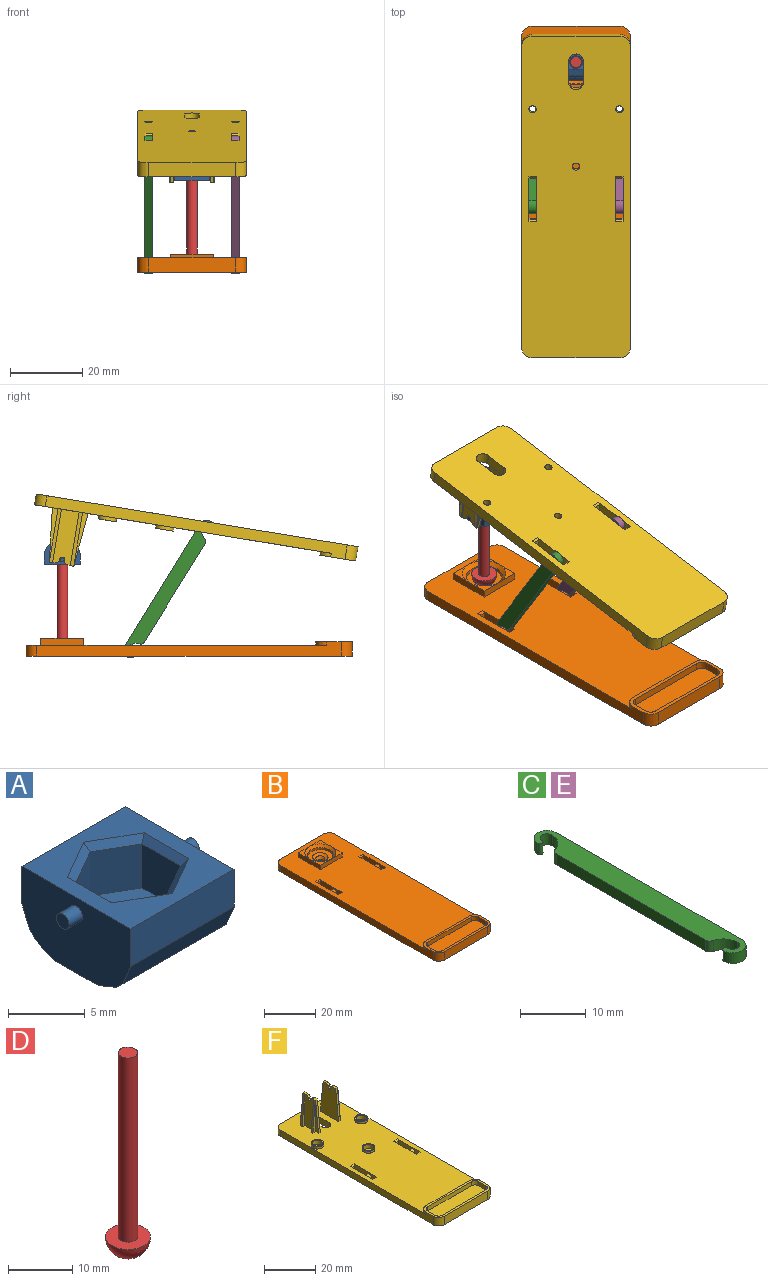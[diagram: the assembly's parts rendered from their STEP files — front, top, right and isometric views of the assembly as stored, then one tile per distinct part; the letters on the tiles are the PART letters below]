
ASSEMBLY  parts=6 mates=8
PART A: 30 faces, bbox 12x10x6 mm
  f0: plane 10x9.5mm, normal (0,0,1), area 51.6mm2, adj f3,f4,f5,f6,f24,f25,f26,f27
  f1: plane 1.15x1.15mm, normal (-1,0,0), area 1mm2, adj f2
  f2: cylinder r=0.57mm len=1.25mm, axis (1,0,0), area 4.5mm2, adj f1,f3
  f3: plane 10x6mm, normal (-1,0,0), area 53.5mm2, adj f0,f2,f4,f6,f7,f10,f11,f19
  f4: plane 9.5x3mm, normal (0,-1,0), area 28.5mm2, adj f0,f3,f5,f22
  f5: plane 10x6mm, normal (1,0,0), area 53.5mm2, adj f0,f4,f6,f7,f9,f10,f11,f19
  f6: plane 9.5x3mm, normal (0,1,0), area 28.5mm2, adj f0,f3,f5,f19
  f7: plane 9.5x4mm, normal (0,0,-1), area 28.4mm2, adj f3,f5,f20,f21,f23
  f8: plane 1.15x1.15mm, normal (1,0,0), area 1mm2, adj f9
  f9: cylinder r=0.57mm len=1.25mm, axis (1,0,0), area 4.5mm2, adj f5,f8
  f10: plane 9.5x0.59mm, normal (0,0.71,-0.71), area 7.9mm2, adj f3,f5,f19,f20
  f11: plane 9.5x0.59mm, normal (0,-0.71,-0.71), area 7.9mm2, adj f3,f5,f21,f22
  f12: plane 3.5x3.04mm, normal (-0.5,-0.87,0), area 12.3mm2, adj f13,f17,f18,f26
  f13: plane 3.5x3.04mm, normal (0.5,-0.87,0), area 12.3mm2, adj f12,f14,f18,f28
  f14: plane 3.51x3.5mm, normal (1,0,0), area 12.3mm2, adj f13,f15,f18,f29
  f15: plane 3.5x3.04mm, normal (0.5,0.87,0), area 12.3mm2, adj f14,f16,f18,f27
  f16: plane 3.5x3.04mm, normal (-0.5,0.87,0), area 12.3mm2, adj f15,f17,f18,f25
  f17: plane 3.51x3.5mm, normal (-1,0,0), area 12.3mm2, adj f12,f16,f18,f24
  f18: plane 7.02x6.08mm, normal (0,0,1), area 22.4mm2, adj f12,f13,f14,f15,f16,f17,f23
  f19: plane 9.5x1.71mm, normal (0,0.92,-0.38), area 17.6mm2, adj f3,f5,f6,f10
  f20: plane 9.5x1.71mm, normal (0,0.38,-0.92), area 17.6mm2, adj f3,f5,f7,f10
  f21: plane 9.5x1.71mm, normal (0,-0.38,-0.92), area 17.6mm2, adj f3,f5,f7,f11
  f22: plane 9.5x1.71mm, normal (0,-0.92,-0.38), area 17.6mm2, adj f3,f4,f5,f11
  f23: cylinder r=1.75mm len=3.5mm, axis (0,0,1), area 22mm2, adj f7,f18
  f24: plane 4.09x0.5mm, normal (-0.71,0,0.71), area 2.7mm2, adj f0,f17,f25,f26
  f25: plane 3.54x2.33mm, normal (-0.35,0.61,0.71), area 2.7mm2, adj f0,f16,f24,f27
  f26: plane 3.54x2.33mm, normal (-0.35,-0.61,0.71), area 2.7mm2, adj f0,f12,f24,f28
  f27: plane 3.54x2.33mm, normal (0.35,0.61,0.71), area 2.7mm2, adj f0,f15,f25,f29
  f28: plane 3.54x2.33mm, normal (0.35,-0.61,0.71), area 2.7mm2, adj f0,f13,f26,f29
  f29: plane 4.09x0.5mm, normal (0.71,0,0.71), area 2.7mm2, adj f0,f14,f27,f28
PART B: 56 faces, bbox 30x90x5 mm
  f0: plane 83x30mm, normal (0,0,1), area 2202.2mm2, adj f6,f8,f9,f12,f13,f14,f15,f16
  f1: plane 90x30mm, normal (0,0,-1), area 2631.5mm2, adj f6,f7,f8,f9,f10,f11,f12,f13
  f2: sphere r=5mm, area 21mm2, adj f32,f36
  f3: plane 6x6mm, normal (0,0,1), area 7.7mm2, adj f29,f30,f34
  f4: plane 6x6mm, normal (0,0,1), area 7.7mm2, adj f28,f29,f34
  f5: plane 6x6mm, normal (0,0,1), area 7.7mm2, adj f27,f28,f34
  f6: plane 84x4mm, normal (-1,0,0), area 256mm2, adj f0,f1,f10,f13,f16,f25
  f7: plane 24x4mm, normal (0,-1,0), area 96mm2, adj f1,f10,f11,f25
  f8: plane 84x4mm, normal (1,0,0), area 256mm2, adj f0,f1,f11,f12,f14,f25
  f9: plane 24x3mm, normal (0,1,0), area 72mm2, adj f0,f1,f12,f13
  f10: cylinder r=3mm len=4mm, axis (0,0,-1), area 18.8mm2, adj f1,f6,f7,f25
  f11: cylinder r=3mm len=4mm, axis (0,0,1), area 18.8mm2, adj f1,f7,f8,f25
  f12: cylinder r=3mm len=3mm, axis (0,0,-1), area 14.1mm2, adj f0,f1,f8,f9
  f13: cylinder r=3mm len=3mm, axis (0,0,1), area 14.1mm2, adj f0,f1,f6,f9
  f14: cylinder r=3mm len=3mm, axis (0,0,-1), area 4.7mm2, adj f0,f8,f15,f25
  f15: plane 24x1mm, normal (0,1,0), area 24mm2, adj f0,f14,f16,f25
  f16: cylinder r=3mm len=3mm, axis (0,0,-1), area 4.7mm2, adj f0,f6,f15,f25
  f17: plane 4x2mm, normal (-1,0,0), area 8mm2, adj f18,f24,f25,f26
  f18: cylinder r=2mm len=2mm, axis (0,0,-1), area 6.3mm2, adj f17,f19,f25,f26
  f19: plane 24x2mm, normal (0,1,0), area 48mm2, adj f18,f20,f25,f26
  f20: cylinder r=2mm len=2mm, axis (0,0,-1), area 6.3mm2, adj f19,f21,f25,f26
  f21: plane 4x2mm, normal (1,0,0), area 8mm2, adj f20,f22,f25,f26
  f22: cylinder r=2mm len=2mm, axis (0,0,-1), area 6.3mm2, adj f21,f23,f25,f26
  f23: plane 24x2mm, normal (0,-1,0), area 48mm2, adj f22,f24,f25,f26
  f24: cylinder r=2mm len=2mm, axis (0,0,-1), area 6.3mm2, adj f17,f23,f25,f26
  f25: plane 30x10mm, normal (0,0,1), area 71.7mm2, adj f6,f7,f8,f10,f11,f14,f15,f16
  f26: plane 28x8mm, normal (0,0,1), area 220.6mm2, adj f17,f18,f19,f20,f21,f22,f23,f24
  f27: plane 12x2mm, normal (0,1,0), area 24mm2, adj f0,f5,f28,f30,f31
  f28: plane 12x2mm, normal (-1,0,0), area 24mm2, adj f0,f4,f5,f27,f29
  f29: plane 12x2mm, normal (0,-1,0), area 24mm2, adj f0,f3,f4,f28,f30
  f30: plane 12x2mm, normal (1,0,0), area 24mm2, adj f0,f3,f27,f29,f31
  f31: plane 6x6mm, normal (0,0,1), area 7.7mm2, adj f27,f30,f34
  f32: plane 10x10mm, normal (0,0,1), area 50.3mm2, adj f2,f33
  f33: cylinder r=5mm len=10mm, axis (0,0,-1), area 31.4mm2, adj f32,f34
  f34: cone r=6mm half-angle=45deg, axis (0,0,1), area 48.9mm2, adj f3,f4,f5,f31,f33
  f35: cylinder r=1mm len=2mm, axis (0,0,1), area 4.3mm2, adj f36,f37
  f36: cone r=1.79mm half-angle=34.5deg, axis (0,0,1), area 12.2mm2, adj f2,f35
  f37: cone r=1mm half-angle=45deg, axis (0,0,-1), area 5.6mm2, adj f1,f35
  f38: plane 2.15x2mm, normal (0,-1,0), area 4.3mm2, adj f39,f40,f52,f53
  f39: plane 12.5x3mm, normal (-1,0,0), area 31.9mm2, adj f0,f1,f38,f41,f47,f52,f53,f54
  f40: plane 12.5x3mm, normal (1,0,0), area 31.9mm2, adj f0,f1,f38,f41,f47,f52,f53,f54
  f41: plane 2.15x2mm, normal (0,1,0), area 4.3mm2, adj f39,f40,f54,f55
  f42: plane 2.15x2mm, normal (0,1,0), area 4.3mm2, adj f43,f45,f49,f50
  f43: plane 12.5x3mm, normal (-1,0,0), area 31.9mm2, adj f0,f1,f42,f44,f46,f48,f49,f50
  f44: plane 2.15x2mm, normal (0,-1,0), area 4.3mm2, adj f43,f45,f48,f51
  f45: plane 12.5x3mm, normal (1,0,0), area 31.9mm2, adj f0,f1,f42,f44,f46,f48,f49,f50
  f46: cylinder r=1mm len=2.15mm, axis (-1,0,0), area 13.5mm2, adj f43,f45
  f47: cylinder r=1mm len=2.15mm, axis (-1,0,0), area 13.5mm2, adj f39,f40
  f48: plane 2.15x0.5mm, normal (0,-0.71,0.71), area 1.5mm2, adj f0,f43,f44,f45
  f49: plane 2.15x0.5mm, normal (0,0.71,0.71), area 1.5mm2, adj f0,f42,f43,f45
  f50: plane 2.15x0.5mm, normal (0,0.71,-0.71), area 1.5mm2, adj f1,f42,f43,f45
  f51: plane 2.15x0.5mm, normal (0,-0.71,-0.71), area 1.5mm2, adj f1,f43,f44,f45
  f52: plane 2.15x0.5mm, normal (0,-0.71,-0.71), area 1.5mm2, adj f1,f38,f39,f40
  f53: plane 2.15x0.5mm, normal (0,-0.71,0.71), area 1.5mm2, adj f0,f38,f39,f40
  f54: plane 2.15x0.5mm, normal (0,0.71,-0.71), area 1.5mm2, adj f1,f39,f40,f41
  f55: plane 2.15x0.5mm, normal (0,0.71,0.71), area 1.5mm2, adj f0,f39,f40,f41
PART C: 14 faces, bbox 4x44x2 mm
  f0: cylinder r=1.07mm len=2.15mm, axis (0,0,-1), area 6.8mm2, adj f1,f9,f10,f11
  f1: cylinder r=3.08mm len=2.98mm, axis (0,0,-1), area 8.1mm2, adj f0,f10,f11,f12
  f2: plane 32.1x2mm, normal (-1,0,0), area 64.2mm2, adj f10,f11,f12,f13
  f3: cylinder r=3.08mm len=2.98mm, axis (0,0,-1), area 8.1mm2, adj f4,f10,f11,f13
  f4: cylinder r=1.07mm len=2.15mm, axis (0,0,-1), area 6.8mm2, adj f3,f5,f10,f11
  f5: cylinder r=0.46mm len=2mm, axis (0,0,-1), area 2.9mm2, adj f4,f6,f10,f11
  f6: cylinder r=2mm len=4mm, axis (0,0,-1), area 12.6mm2, adj f5,f7,f10,f11
  f7: plane 40x2mm, normal (1,0,0), area 80mm2, adj f6,f8,f10,f11
  f8: cylinder r=2mm len=4mm, axis (0,0,-1), area 12.6mm2, adj f7,f9,f10,f11
  f9: cylinder r=0.46mm len=2mm, axis (0,0,-1), area 2.9mm2, adj f0,f8,f10,f11
  f10: plane 44x4mm, normal (0,0,1), area 154.5mm2, adj f0,f1,f2,f3,f4,f5,f6,f7
  f11: plane 44x4mm, normal (0,0,-1), area 154.5mm2, adj f0,f1,f2,f3,f4,f5,f6,f7
  f12: cylinder r=1mm len=2mm, axis (0,0,-1), area 2.6mm2, adj f1,f2,f10,f11
  f13: cylinder r=1mm len=2mm, axis (0,0,-1), area 2.6mm2, adj f2,f3,f10,f11
PART D: 4 faces, bbox 7x7x38.5 mm
  f0: cylinder r=1.5mm len=35mm, axis (0,0,-1), area 329.9mm2, adj f1,f3
  f1: plane 3x3mm, normal (0,0,1), area 7.1mm2, adj f0
  f2: sphere r=3.5mm, area 77mm2, adj f3
  f3: plane 7x7mm, normal (0,0,1), area 31.4mm2, adj f0,f2
PART E: same geometry as C
PART F: 94 faces, bbox 30x90x18 mm
  f0: plane 83x30mm, normal (0,0,1), area 2225.1mm2, adj f2,f3,f4,f5,f8,f10,f11,f14
  f1: plane 90x30mm, normal (0,0,-1), area 2592.5mm2, adj f8,f9,f10,f11,f12,f13,f14,f15
  f2: plane 15x4.95mm, normal (-1,0,0), area 70.9mm2, adj f0,f40,f43,f44,f51,f56
  f3: plane 15x1.58mm, normal (-1,0,0), area 11.8mm2, adj f0,f29,f52
  f4: plane 15x1.58mm, normal (1,0,0), area 11.8mm2, adj f0,f36,f50
  f5: plane 15x4.95mm, normal (1,0,0), area 70.9mm2, adj f0,f39,f41,f42,f47,f48
  f6: plane 1.19x0.95mm, normal (0,0,1), area 1.1mm2, adj f30,f31,f43,f54,f55,f56
  f7: plane 1.19x0.95mm, normal (0,0,1), area 1.1mm2, adj f34,f35,f42,f45,f46,f47
  f8: plane 84x4mm, normal (-1,0,0), area 256mm2, adj f0,f1,f12,f15,f18,f27
  f9: plane 24x4mm, normal (0,-1,0), area 96mm2, adj f1,f12,f13,f27
  f10: plane 84x4mm, normal (1,0,0), area 256mm2, adj f0,f1,f13,f14,f16,f27
  f11: plane 24x3mm, normal (0,1,0), area 72mm2, adj f0,f1,f14,f15
  f12: cylinder r=3mm len=4mm, axis (0,0,-1), area 18.8mm2, adj f1,f8,f9,f27
  f13: cylinder r=3mm len=4mm, axis (0,0,1), area 18.8mm2, adj f1,f9,f10,f27
  f14: cylinder r=3mm len=3mm, axis (0,0,-1), area 14.1mm2, adj f0,f1,f10,f11
  f15: cylinder r=3mm len=3mm, axis (0,0,1), area 14.1mm2, adj f0,f1,f8,f11
  f16: cylinder r=3mm len=3mm, axis (0,0,-1), area 4.7mm2, adj f0,f10,f17,f27
  f17: plane 24x1mm, normal (0,1,0), area 24mm2, adj f0,f16,f18,f27
  f18: cylinder r=3mm len=3mm, axis (0,0,-1), area 4.7mm2, adj f0,f8,f17,f27
  f19: plane 4x2mm, normal (-1,0,0), area 8mm2, adj f20,f26,f27,f28
  f20: cylinder r=2mm len=2mm, axis (0,0,-1), area 6.3mm2, adj f19,f21,f27,f28
  f21: plane 24x2mm, normal (0,1,0), area 48mm2, adj f20,f22,f27,f28
  f22: cylinder r=2mm len=2mm, axis (0,0,-1), area 6.3mm2, adj f21,f23,f27,f28
  f23: plane 4x2mm, normal (1,0,0), area 8mm2, adj f22,f24,f27,f28
  f24: cylinder r=2mm len=2mm, axis (0,0,-1), area 6.3mm2, adj f23,f25,f27,f28
  f25: plane 24x2mm, normal (0,-1,0), area 48mm2, adj f24,f26,f27,f28
  f26: cylinder r=2mm len=2mm, axis (0,0,-1), area 6.3mm2, adj f19,f25,f27,f28
  f27: plane 30x10mm, normal (0,0,1), area 71.7mm2, adj f8,f9,f10,f12,f13,f16,f17,f18
  f28: plane 28x8mm, normal (0,0,1), area 220.6mm2, adj f19,f20,f21,f22,f23,f24,f25,f26
  f29: plane 15x1.58mm, normal (0,-0.99,0.1), area 15.1mm2, adj f0,f3,f30,f33
  f30: plane 15x10mm, normal (1,0,0), area 123.1mm2, adj f0,f6,f29,f31,f33,f40,f43,f44
  f31: plane 15x1.58mm, normal (0,0.99,0.1), area 15.1mm2, adj f0,f6,f30,f32
  f32: plane 15x1.58mm, normal (-1,0,0), area 11.8mm2, adj f0,f31,f55
  f33: plane 1.19x0.95mm, normal (0,0,1), area 1.1mm2, adj f29,f30,f44,f51,f52,f53
  f34: plane 15x1.58mm, normal (0,0.99,0.1), area 15.1mm2, adj f0,f7,f35,f37
  f35: plane 15x10mm, normal (-1,0,0), area 123.1mm2, adj f0,f7,f34,f36,f38,f39,f41,f42
  f36: plane 15x1.58mm, normal (0,-0.99,0.1), area 15.1mm2, adj f0,f4,f35,f38
  f37: plane 15x1.58mm, normal (1,0,0), area 11.8mm2, adj f0,f34,f45
  f38: plane 1.19x0.95mm, normal (0,0,1), area 1.1mm2, adj f35,f36,f41,f48,f49,f50
  f39: cylinder r=0.75mm len=1.5mm, axis (1,0,0), area 3.5mm2, adj f5,f35,f41,f42
  f40: cylinder r=0.75mm len=1.5mm, axis (1,0,0), area 3.5mm2, adj f2,f30,f43,f44
  f41: cylinder r=3mm len=1.95mm, axis (1,0,0), area 2.1mm2, adj f5,f35,f38,f39
  f42: cylinder r=3mm len=1.95mm, axis (1,0,0), area 2.1mm2, adj f5,f7,f35,f39
  f43: cylinder r=3mm len=1.95mm, axis (1,0,0), area 2.1mm2, adj f2,f6,f30,f40
  f44: cylinder r=3mm len=1.95mm, axis (1,0,0), area 2.1mm2, adj f2,f30,f33,f40
  f45: plane 15x1.5mm, normal (0,1,0), area 12.7mm2, adj f0,f7,f37,f46
  f46: plane 15x1.31mm, normal (1,0,0.09), area 14.3mm2, adj f0,f7,f45,f47
  f47: plane 15x1.5mm, normal (0,-1,0), area 12.7mm2, adj f0,f5,f7,f46
  f48: plane 15x1.5mm, normal (0,1,0), area 12.7mm2, adj f0,f5,f38,f49
  f49: plane 15x1.31mm, normal (1,0,0.09), area 14.3mm2, adj f0,f38,f48,f50
  f50: plane 15x1.5mm, normal (0,-1,0), area 12.7mm2, adj f0,f4,f38,f49
  f51: plane 15x1.5mm, normal (0,1,0), area 12.7mm2, adj f0,f2,f33,f53
  f52: plane 15x1.5mm, normal (0,-1,0), area 12.7mm2, adj f0,f3,f33,f53
  f53: plane 15x1.31mm, normal (-1,0,0.09), area 14.3mm2, adj f0,f33,f51,f52
  f54: plane 15x1.31mm, normal (-1,0,0.09), area 14.3mm2, adj f0,f6,f55,f56
  f55: plane 15x1.5mm, normal (0,1,0), area 12.7mm2, adj f0,f6,f32,f54
  f56: plane 15x1.5mm, normal (0,-1,0), area 12.7mm2, adj f0,f2,f6,f54
  f57: plane 2.15x2mm, normal (0,-1,0), area 4.3mm2, adj f63,f64,f71,f74
  f58: plane 2.15x2mm, normal (0,1,0), area 4.3mm2, adj f59,f61,f68,f70
  f59: plane 12.5x3mm, normal (-1,0,0), area 31.9mm2, adj f0,f1,f58,f60,f66,f68,f70,f72
  f60: plane 2.15x2mm, normal (0,-1,0), area 4.3mm2, adj f59,f61,f72,f73
  f61: plane 12.5x3mm, normal (1,0,0), area 31.9mm2, adj f0,f1,f58,f60,f66,f68,f70,f72
  f62: plane 2.15x2mm, normal (0,1,0), area 4.3mm2, adj f63,f64,f67,f69
  f63: plane 12.5x3mm, normal (-1,0,0), area 31.9mm2, adj f0,f1,f57,f62,f65,f67,f69,f71
  f64: plane 12.5x3mm, normal (1,0,0), area 31.9mm2, adj f0,f1,f57,f62,f65,f67,f69,f71
  f65: cylinder r=1mm len=2.15mm, axis (1,0,0), area 13.5mm2, adj f63,f64
  f66: cylinder r=1mm len=2.15mm, axis (1,0,0), area 13.5mm2, adj f59,f61
  f67: plane 2.15x0.5mm, normal (0,0.71,-0.71), area 1.5mm2, adj f1,f62,f63,f64
  f68: plane 2.15x0.5mm, normal (0,0.71,-0.71), area 1.5mm2, adj f1,f58,f59,f61
  f69: plane 2.15x0.5mm, normal (0,0.71,0.71), area 1.5mm2, adj f0,f62,f63,f64
  f70: plane 2.15x0.5mm, normal (0,0.71,0.71), area 1.5mm2, adj f0,f58,f59,f61
  f71: plane 2.15x0.5mm, normal (0,-0.71,-0.71), area 1.5mm2, adj f1,f57,f63,f64
  f72: plane 2.15x0.5mm, normal (0,-0.71,-0.71), area 1.5mm2, adj f1,f59,f60,f61
  f73: plane 2.15x0.5mm, normal (0,-0.71,0.71), area 1.5mm2, adj f0,f59,f60,f61
  f74: plane 2.15x0.5mm, normal (0,-0.71,0.71), area 1.5mm2, adj f0,f57,f63,f64
  f75: cylinder r=2mm len=4mm, axis (0,0,1), area 18.8mm2, adj f0,f1,f76,f78
  f76: plane 6x3mm, normal (-1,0,0), area 18mm2, adj f0,f1,f75,f77
  f77: cylinder r=2mm len=4mm, axis (0,0,1), area 18.8mm2, adj f0,f1,f76,f78
  f78: plane 6x3mm, normal (1,0,0), area 18mm2, adj f0,f1,f75,f77
  f79: cylinder r=1mm len=2mm, axis (0,0,1), area 12.6mm2, adj f1,f87
  f80: cylinder r=1mm len=2mm, axis (0,0,1), area 12.6mm2, adj f1,f85
  f81: cylinder r=1mm len=2mm, axis (0,0,1), area 12.6mm2, adj f1,f83
  f82: cylinder r=2mm len=4mm, axis (0,0,1), area 25.1mm2, adj f83,f91
  f83: plane 4x4mm, normal (0,0,1), area 9.4mm2, adj f81,f82
  f84: cylinder r=2mm len=4mm, axis (0,0,1), area 25.1mm2, adj f85,f89
  f85: plane 4x4mm, normal (0,0,1), area 9.4mm2, adj f80,f84
  f86: cylinder r=2mm len=4mm, axis (0,0,1), area 25.1mm2, adj f87,f93
  f87: plane 4x4mm, normal (0,0,1), area 9.4mm2, adj f79,f86
  f88: cylinder r=2.5mm len=5mm, axis (0,0,-1), area 15.7mm2, adj f0,f89
  f89: plane 5x5mm, normal (0,0,1), area 7.1mm2, adj f84,f88
  f90: cylinder r=2.5mm len=5mm, axis (0,0,-1), area 15.7mm2, adj f0,f91
  f91: plane 5x5mm, normal (0,0,1), area 7.1mm2, adj f82,f90
  f92: cylinder r=2.5mm len=5mm, axis (0,0,-1), area 15.7mm2, adj f0,f93
  f93: plane 5x5mm, normal (0,0,1), area 7.1mm2, adj f86,f92
PLACE A rot(axis=(0,-1,0),180deg) t=(45.48,-22.52,60.65)mm
PLACE B t=(11.18,-22.52,17.29)mm fixed
PLACE C rot(axis=(-0.44,-0.79,0.44),103.7deg) t=(-2.67,1.85,78.4)mm
PLACE D rot(axis=(0,0,-1),90deg) t=(-34.46,-39.26,22.29)mm
PLACE E rot(axis=(0.66,0.37,0.66),139.7deg) t=(19.33,32.06,29.48)mm
PLACE F rot(axis=(0,-1,-0.08),180deg) t=(45.48,-24.7,54.05)mm
MATE revolute F.f39 <-> A.f2  axis (-1,0,0) through (2.33,16.96,43.9)mm
MATE cylindrical A.f23 <-> D.f0  axis (0,0,1) through (8.33,16.96,48.65)mm
MATE parallel B.f33 <-> A.f23  axis (0,0,1) through (8.33,16.96,22.29)mm
MATE revolute C.f4 <-> F.f65  axis (-1,0,0) through (-4.67,-22.91,52.83)mm
MATE revolute E.f0 <-> F.f65  axis (1,0,0) through (21.33,-22.91,52.83)mm
MATE revolute C.f0 <-> B.f46  axis (-1,0,0) through (-4.67,-1.89,18.79)mm
MATE revolute E.f4 <-> B.f46  axis (1,0,0) through (21.33,-1.89,18.79)mm
MATE ball D.f0 <-> B.f33  axis (0,0,1) through (8.33,16.96,22.29)mm
